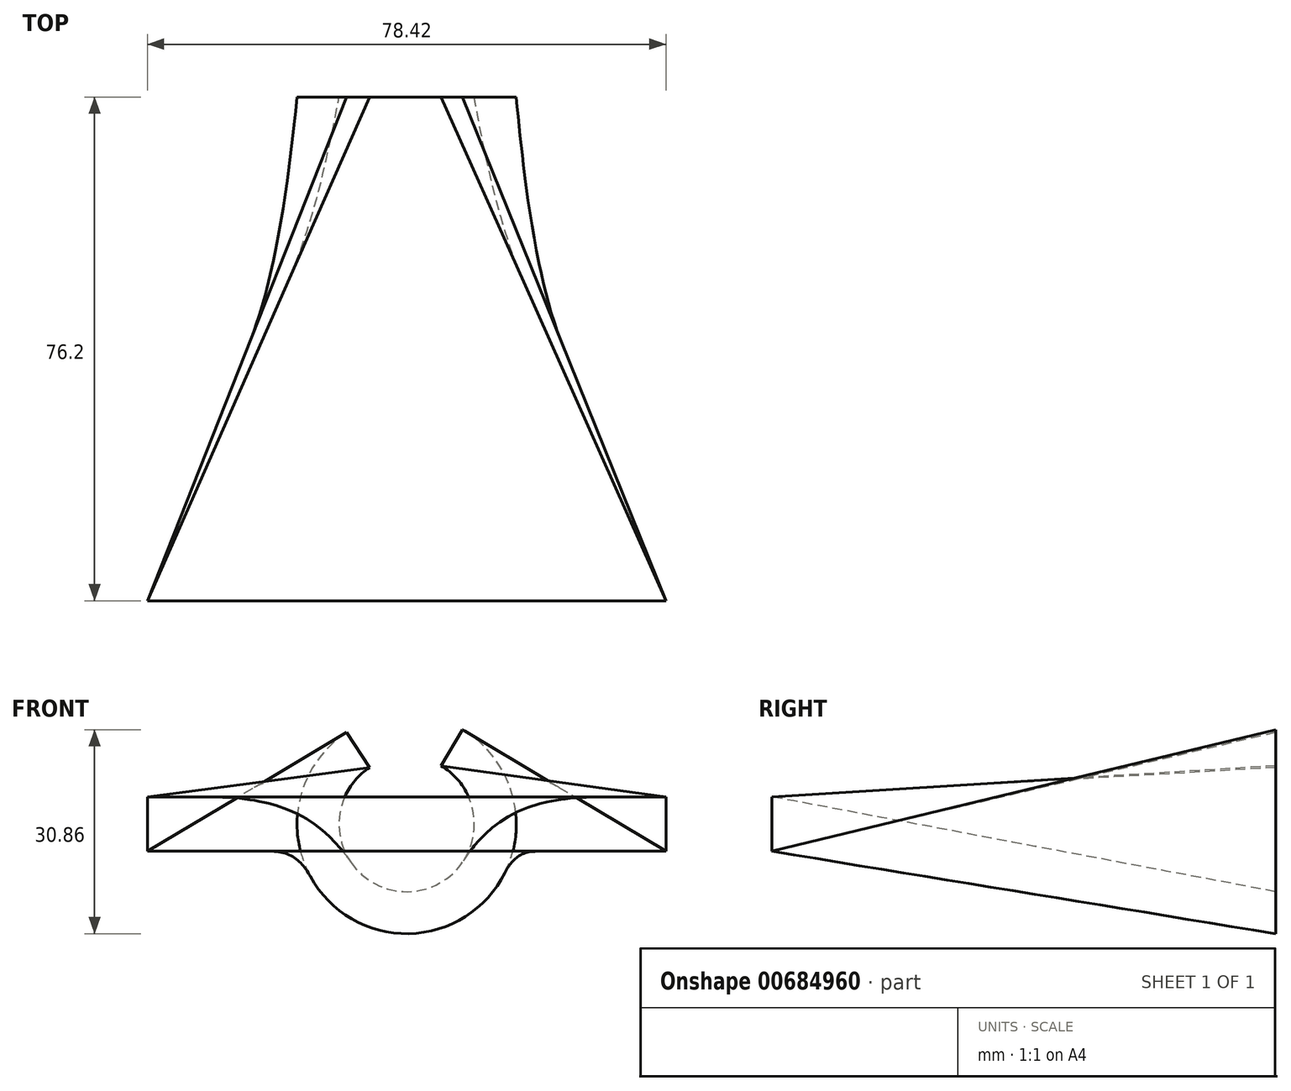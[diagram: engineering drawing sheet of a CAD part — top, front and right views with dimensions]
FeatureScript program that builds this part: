
annotation { "Feature Type Name" : "Feature", "Feature Type Description" : "" }
export const myFeature = defineFeature(function(context is Context, id is Id, definition is map)
    precondition{}
    {
        {
            var Q0;
            Q0=qCreatedBy(makeId("Front.planeOp"),FACE);
            var sketch = newSketch(context, id + "F0", { "sketchPlane" : qUnion([Q0])});
            skArc(sketch, "E0", {"start": v(-5.63, 8.55) * mm, "mid": v(0.25, -10.23) * mm, "end": v(5.2, 8.81) * mm});
            skArc(sketch, "E1.0", {"start": v(-9.12, 13.85) * mm, "mid": v(0.4, -16.58) * mm, "end": v(8.43, 14.28) * mm});
            skLineSegment(sketch, "E2", {"start": v(-9.12, 13.85) * mm, "end": v(-5.63, 8.55) * mm});
            skLineSegment(sketch, "E3", {"start": v(8.43, 14.28) * mm, "end": v(5.2, 8.81) * mm});
            skSolve(sketch);
        }
        {
            var Q0;
            Q0=qCreatedBy(makeId("Front.planeOp"),FACE);
            cPlane(context, id + "F1", {"entities" : qUnion([Q0]), "cplaneType" : CPlaneType.OFFSET, "offset" : 76.2 * mm, "width" : 152.4 * mm, "height" : 152.4 * mm});
        }
        {
            var Q0;
            Q0=qCreatedBy(id+"F1.planeOp",FACE);
            var sketch = newSketch(context, id + "F2", { "sketchPlane" : qUnion([Q0])});
            skLineSegment(sketch, "E4.bottom", {"start": v(-39.21, 4.12) * mm, "end": v(39.21, 4.12) * mm});
            skLineSegment(sketch, "E4.top", {"start": v(-39.21, -4.12) * mm, "end": v(39.21, -4.12) * mm});
            skLineSegment(sketch, "E4.left", {"start": v(-39.21, 4.12) * mm, "end": v(-39.21, -4.12) * mm});
            skLineSegment(sketch, "E4.right", {"start": v(39.21, 4.12) * mm, "end": v(39.21, -4.12) * mm});
            skPoint(sketch, "E4.middle", {"position": v(0, 0) * mm});
            skSolve(sketch);
        }
        {
            var Q0;
            Q0=makeQuery(id+"F0.imprint","IMPRINT",FACE,{"disambiguationData":[TD([[makeQuery(id+"F0.imprint","IMPRINT",EDGE,{"derivedFrom":sQuery(id+"F0.wireOp",EDGE,"E0")}),-1.0]])]});
            var Q1;
            Q1=makeQuery(id+"F2.imprint","IMPRINT",FACE,{"disambiguationData":[TD([[makeQuery(id+"F2.imprint","IMPRINT",EDGE,{"derivedFrom":sQuery(id+"F2.wireOp",EDGE,"E4.bottom")}),-1.0]])]});
            loft(context, id + "F3", {"bodyType" : ToolBodyType.SURFACE, "wireProfilesArray" : [{ "wireProfileEntities" : qUnion([Q0]) }, { "wireProfileEntities" : qUnion([Q1]) }]});
        }
    });
